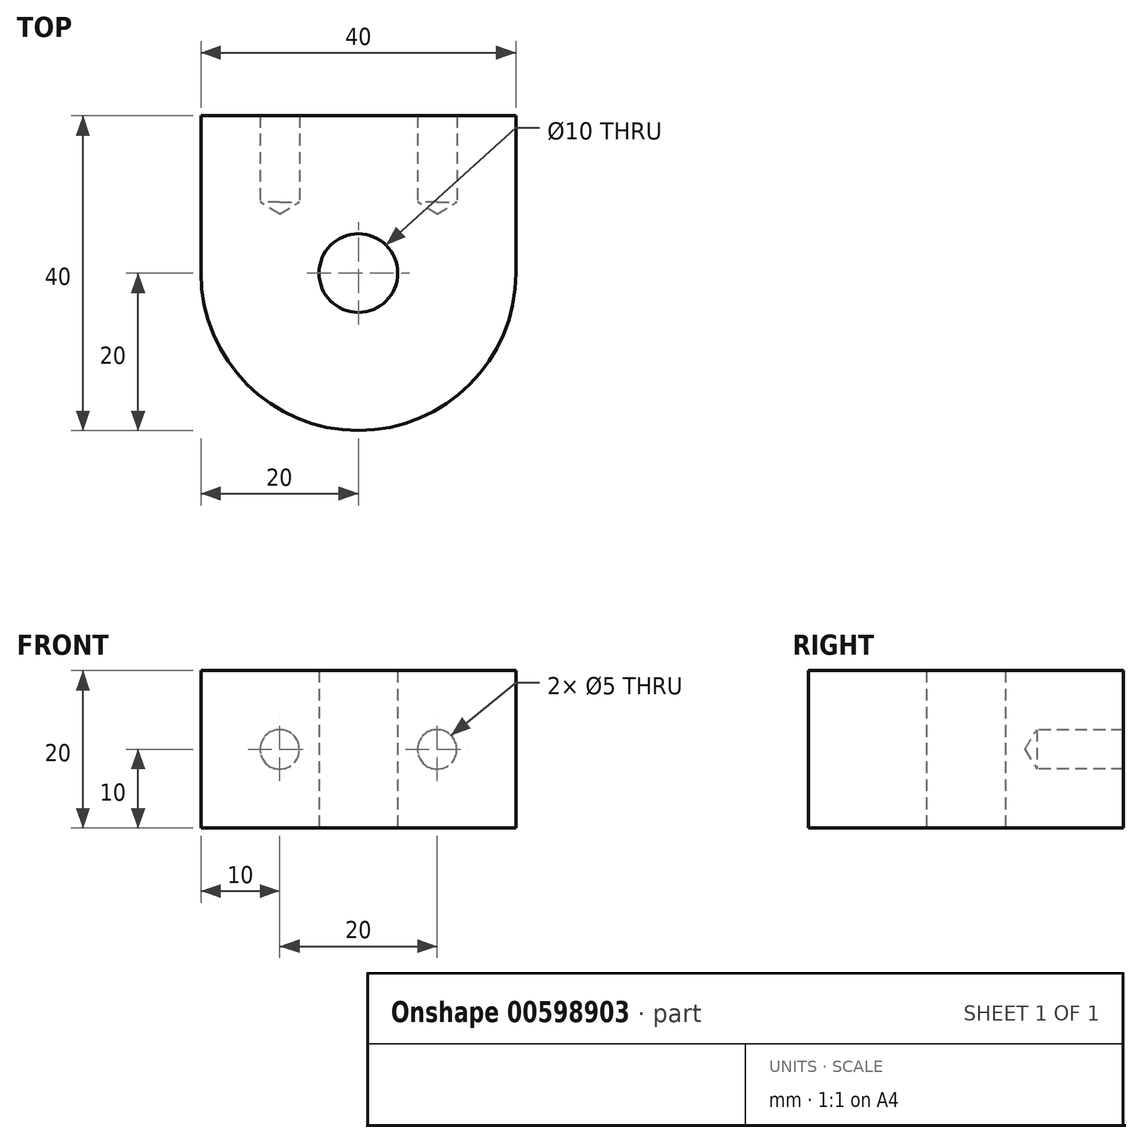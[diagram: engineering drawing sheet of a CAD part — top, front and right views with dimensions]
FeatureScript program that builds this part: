
annotation { "Feature Type Name" : "Feature", "Feature Type Description" : "" }
export const myFeature = defineFeature(function(context is Context, id is Id, definition is map)
    precondition{}
    {
        {
            var Q0;
            Q0=qCreatedBy(makeId("Top.planeOp"),FACE);
            var sketch = newSketch(context, id + "F0", { "sketchPlane" : qUnion([Q0])});
            skLineSegment(sketch, "E0.bottom", {"start": v(0, 0) * mm, "end": v(40, 0) * mm});
            skLineSegment(sketch, "E0.top", {"start": v(0, -20) * mm, "end": v(40, -20) * mm, "construction": true});
            skLineSegment(sketch, "E0.left", {"start": v(0, 0) * mm, "end": v(0, -20) * mm});
            skLineSegment(sketch, "E0.right", {"start": v(40, 0) * mm, "end": v(40, -20) * mm});
            skArc(sketch, "E1", {"start": v(0, -20) * mm, "mid": v(20, -40) * mm, "end": v(40, -20) * mm});
            skCircle(sketch, "E2", {"center": v(20, -20) * mm, "radius": 5 * mm});
            skSolve(sketch);
        }
        {
            var Q0;
            Q0=makeQuery(id+"F0.imprint","IMPRINT",FACE,{"disambiguationData":[TD([[makeQuery(id+"F0.imprint","IMPRINT",EDGE,{"derivedFrom":sQuery(id+"F0.wireOp",EDGE,"E0.bottom")}),-1.0]])]});
            extrude(context, id + "F1", {"entities" : qUnion([Q0]), "depth" : 20 * mm, "offsetDistance" : 25 * mm});
        }
        {
            var Q0;
            Q0=makeQuery(id+"F1.opExtrude","SWEPT_FACE",FACE,{"disambiguationData":[OSD([sQuery(id+"F0.wireOp",EDGE,"E0.bottom")])]});
            var sketch = newSketch(context, id + "F2", { "sketchPlane" : qUnion([Q0])});
            skLineSegment(sketch, "E3", {"start": v(0, 10) * mm, "end": v(-40, 10) * mm, "construction": true});
            skPoint(sketch, "E4", {"position": v(-10, 10) * mm});
            skPoint(sketch, "E5", {"position": v(-30, 10) * mm});
            skSolve(sketch);
        }
        {
            var Q0;
            Q0=sQuery(id+"F2.wireOp",VERTEX,"E4");
            var Q1;
            Q1=sQuery(id+"F2.wireOp",VERTEX,"E5");
            var Q2;
            Q2=makeQuery(id+"F1.opExtrude","SWEPT_BODY",BODY,{"disambiguationData":[OSD([sQuery(id+"F0.wireOp",EDGE,"E0.bottom"),sQuery(id+"F0.wireOp",EDGE,"E0.left"),sQuery(id+"F0.wireOp",EDGE,"E0.right"),sQuery(id+"F0.wireOp",EDGE,"E1"),sQuery(id+"F0.wireOp",EDGE,"E2")])]});
            hole(context, id + "F3", {"style" : HoleStyle.SIMPLE, "endStyle" : HoleEndStyle.BLIND, "holeDiameter" : 5 * mm, "majorDiameter" : 5 * mm, "holeDepth" : 11 * mm, "isTappedThrough" : true, "tappedDepth" : 12 * mm, "tapClearance" : 3, "startFromSketch" : true, "locations" : qUnion([Q0, Q1]), "scope" : qUnion([Q2])});
        }
    });
